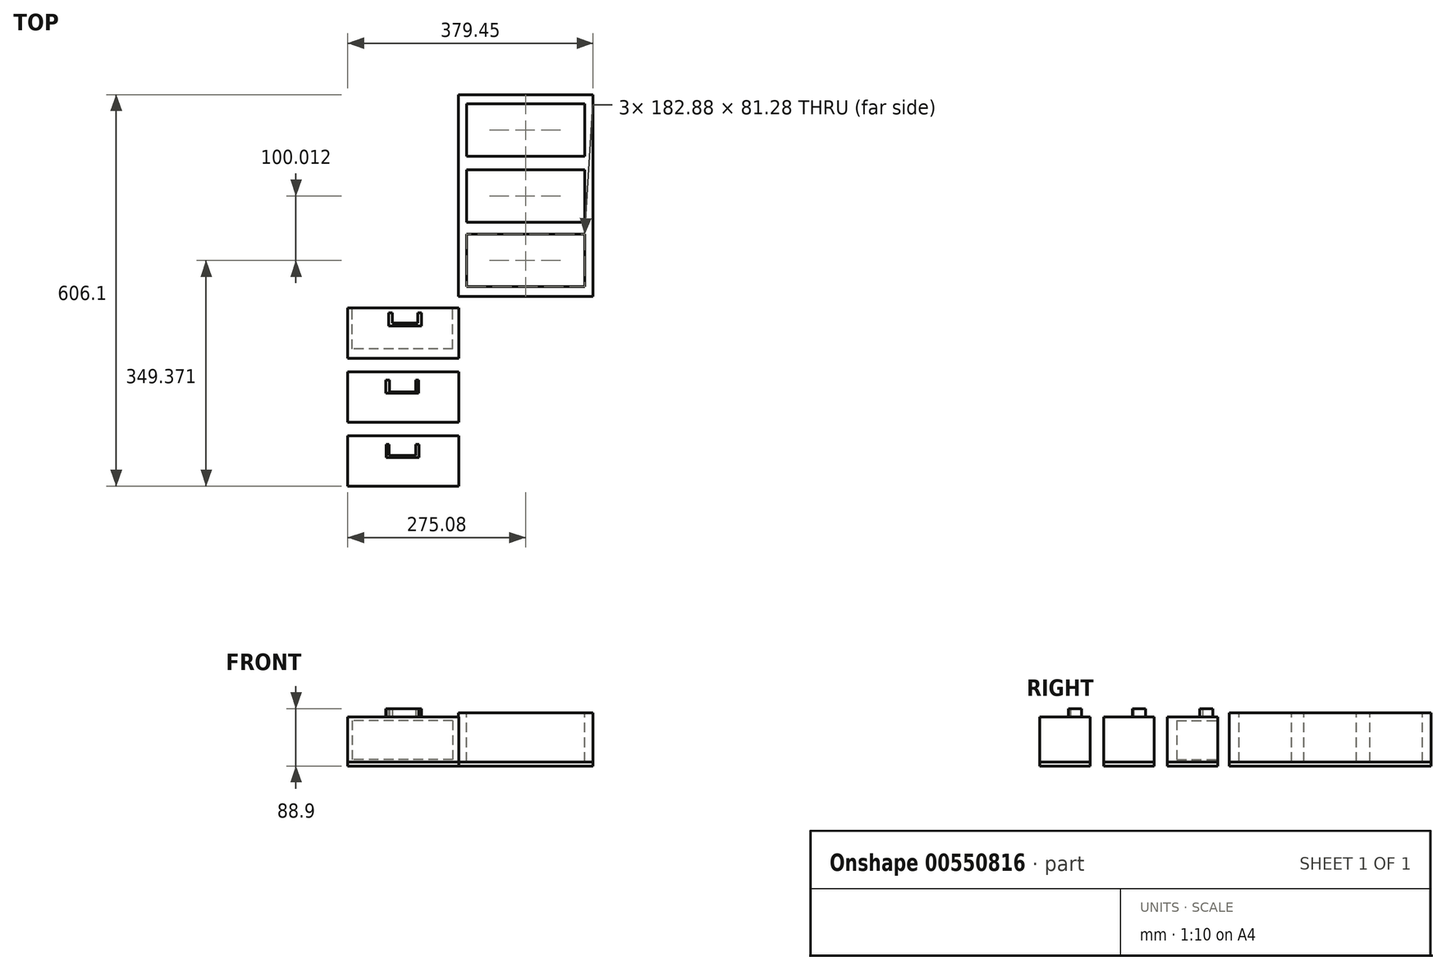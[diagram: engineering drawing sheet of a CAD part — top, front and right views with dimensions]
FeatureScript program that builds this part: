
annotation { "Feature Type Name" : "Feature", "Feature Type Description" : "" }
export const myFeature = defineFeature(function(context is Context, id is Id, definition is map)
    precondition{}
    {
        {
            var Q0;
            Q0=qCreatedBy(makeId("Top.planeOp"),FACE);
            var sketch = newSketch(context, id + "F0", { "sketchPlane" : qUnion([Q0])});
            skPoint(sketch, "E0.middle", {"position": v(0, 0) * mm});
            skLineSegment(sketch, "E1.bottom", {"start": v(208.28, 312.42) * mm, "end": v(0, 312.42) * mm});
            skLineSegment(sketch, "E1.top", {"start": v(208.28, 0) * mm, "end": v(0, 0) * mm});
            skLineSegment(sketch, "E1.left", {"start": v(208.28, 312.42) * mm, "end": v(208.28, 0) * mm});
            skLineSegment(sketch, "E1.right", {"start": v(0, 312.42) * mm, "end": v(0, 0) * mm});
            skLineSegment(sketch, "E2.bottom", {"start": v(12.47, 298.65) * mm, "end": v(195.35, 298.65) * mm});
            skLineSegment(sketch, "E2.top", {"start": v(12.47, 217.37) * mm, "end": v(195.35, 217.37) * mm});
            skLineSegment(sketch, "E2.left", {"start": v(12.47, 298.65) * mm, "end": v(12.47, 217.37) * mm});
            skLineSegment(sketch, "E2.right", {"start": v(195.35, 298.65) * mm, "end": v(195.35, 217.37) * mm});
            skLineSegment(sketch, "E3.bottom", {"start": v(12.47, 196.34) * mm, "end": v(195.35, 196.34) * mm});
            skLineSegment(sketch, "E3.top", {"start": v(12.47, 115.06) * mm, "end": v(195.35, 115.06) * mm});
            skLineSegment(sketch, "E3.left", {"start": v(12.47, 196.34) * mm, "end": v(12.47, 115.06) * mm});
            skLineSegment(sketch, "E3.right", {"start": v(195.35, 196.34) * mm, "end": v(195.35, 115.06) * mm});
            skLineSegment(sketch, "E4.bottom", {"start": v(12.47, 96.33) * mm, "end": v(195.35, 96.33) * mm});
            skLineSegment(sketch, "E4.top", {"start": v(12.47, 15.05) * mm, "end": v(195.35, 15.05) * mm});
            skLineSegment(sketch, "E4.left", {"start": v(12.47, 96.33) * mm, "end": v(12.47, 15.05) * mm});
            skLineSegment(sketch, "E4.right", {"start": v(195.35, 96.33) * mm, "end": v(195.35, 15.05) * mm});
            skSolve(sketch);
        }
        {
            var Q0;
            Q0=makeQuery(id+"F0.imprint","IMPRINT",FACE,{"disambiguationData":[TD([[makeQuery(id+"F0.imprint","IMPRINT",EDGE,{"derivedFrom":sQuery(id+"F0.wireOp",EDGE,"E1.bottom")}),1.0]])]});
            var Q1;
            Q1 = qSketchRegion(id + "F2", true);
            extrude(context, id + "F1", {"entities" : qUnion([Q0, Q1]), "oppositeDirection" : true, "depth" : 76.2 * mm, "offsetDistance" : 25.4 * mm});
        }
        {
            var Q0;
            Q0=makeQuery(id+"F1.opExtrude","CAP_FACE",FACE,{"disambiguationData":[OSD([sQuery(id+"F0.wireOp",EDGE,"E1.bottom"),sQuery(id+"F0.wireOp",EDGE,"E1.top"),sQuery(id+"F0.wireOp",EDGE,"E1.left"),sQuery(id+"F0.wireOp",EDGE,"E1.right")])],"isStart":false});
            var sketch = newSketch(context, id + "F2", { "sketchPlane" : qUnion([Q0])});
            skLineSegment(sketch, "E5.bottom", {"start": v(11.7, 293.68) * mm, "end": v(183.26, 293.68) * mm});
            skLineSegment(sketch, "E5.top", {"start": v(11.7, 215.63) * mm, "end": v(183.26, 215.63) * mm});
            skLineSegment(sketch, "E5.left", {"start": v(11.7, 293.68) * mm, "end": v(11.7, 215.63) * mm});
            skLineSegment(sketch, "E5.right", {"start": v(183.26, 293.68) * mm, "end": v(183.26, 215.63) * mm});
            skLineSegment(sketch, "E6.bottom", {"start": v(11.7, 194.8) * mm, "end": v(183.26, 194.8) * mm});
            skLineSegment(sketch, "E6.top", {"start": v(11.7, 116.74) * mm, "end": v(183.26, 116.74) * mm});
            skLineSegment(sketch, "E6.left", {"start": v(11.7, 194.8) * mm, "end": v(11.7, 116.74) * mm});
            skLineSegment(sketch, "E6.right", {"start": v(183.26, 194.8) * mm, "end": v(183.26, 116.74) * mm});
            skLineSegment(sketch, "E7.bottom", {"start": v(11.7, 95.91) * mm, "end": v(183.26, 95.91) * mm});
            skLineSegment(sketch, "E7.top", {"start": v(11.7, 17.86) * mm, "end": v(183.26, 17.86) * mm});
            skLineSegment(sketch, "E7.left", {"start": v(11.7, 95.91) * mm, "end": v(11.7, 17.86) * mm});
            skLineSegment(sketch, "E7.right", {"start": v(183.26, 95.91) * mm, "end": v(183.26, 17.86) * mm});
            skLineSegment(sketch, "E8.bottom", {"start": v(0, 0) * mm, "end": v(208.28, 0) * mm});
            skLineSegment(sketch, "E8.top", {"start": v(0, -312.42) * mm, "end": v(208.28, -312.42) * mm});
            skLineSegment(sketch, "E8.left", {"start": v(0, 0) * mm, "end": v(0, -312.42) * mm});
            skLineSegment(sketch, "E8.right", {"start": v(208.28, 0) * mm, "end": v(208.28, -312.42) * mm});
            skLineSegment(sketch, "E9.bottom", {"start": v(25.13, 17.86) * mm, "end": v(168.62, 17.86) * mm});
            skSolve(sketch);
        }
        {
            var Q0;
            Q0=makeQuery(id+"F2.imprint","IMPRINT",FACE,{"disambiguationData":[TD([[makeQuery(id+"F2.imprint","IMPRINT",EDGE,{"derivedFrom":sQuery(id+"F2.wireOp",EDGE,"E7.bottom")}),-1.0]])]});
            var Q1;
            Q1=makeQuery(id+"F2.imprint","IMPRINT",FACE,{"disambiguationData":[TD([[makeQuery(id+"F2.imprint","IMPRINT",EDGE,{"derivedFrom":sQuery(id+"F2.wireOp",EDGE,"E6.bottom")}),-1.0]])]});
            var Q2;
            Q2=makeQuery(id+"F2.imprint","IMPRINT",FACE,{"disambiguationData":[TD([[makeQuery(id+"F2.imprint","IMPRINT",EDGE,{"derivedFrom":sQuery(id+"F2.wireOp",EDGE,"E5.bottom")}),-1.0]])]});
            extrude(context, id + "F3", {"entities" : qUnion([Q0, Q1, Q2]), "oppositeDirection" : true, "depth" : 69.85 * mm, "offsetDistance" : 25.4 * mm});
        }
        {
            var Q0;
            Q0 = qSketchRegion(id + "F2", true);
            extrude(context, id + "F4", {"entities" : qUnion([Q0]), "depth" : 6.35 * mm, "offsetDistance" : 25.4 * mm});
        }
        {
            var Q0;
            Q0=makeQuery(id+"F3.opExtrude","CAP_FACE",FACE,{"disambiguationData":[OSD([sQuery(id+"F2.wireOp",EDGE,"E7.bottom"),sQuery(id+"F2.wireOp",EDGE,"E7.top"),sQuery(id+"F2.wireOp",EDGE,"E7.left"),sQuery(id+"F2.wireOp",EDGE,"E7.right")])],"isStart":false});
            var sketch = newSketch(context, id + "F5", { "sketchPlane" : qUnion([Q0])});
            skLineSegment(sketch, "E10.bottom", {"start": v(74.8, -25.28) * mm, "end": v(125.6, -25.28) * mm});
            skLineSegment(sketch, "E10.top", {"start": v(74.8, -45.6) * mm, "end": v(125.6, -45.6) * mm});
            skLineSegment(sketch, "E10.left", {"start": v(74.8, -25.28) * mm, "end": v(74.8, -45.6) * mm});
            skLineSegment(sketch, "E10.right", {"start": v(125.6, -25.28) * mm, "end": v(125.6, -45.6) * mm});
            skLineSegment(sketch, "E11.bottom", {"start": v(80.5, -25.28) * mm, "end": v(119.7, -25.28) * mm});
            skLineSegment(sketch, "E11.top", {"start": v(80.5, -41.56) * mm, "end": v(119.7, -41.56) * mm});
            skLineSegment(sketch, "E11.left", {"start": v(80.5, -25.28) * mm, "end": v(80.5, -41.56) * mm});
            skLineSegment(sketch, "E11.right", {"start": v(119.7, -25.28) * mm, "end": v(119.7, -41.56) * mm});
            skSolve(sketch);
        }
        {
            var Q0;
            Q0=makeQuery(id+"F5.imprint","IMPRINT",FACE,{"disambiguationData":[TD([[makeQuery(id+"F5.imprint","IMPRINT",EDGE,{"derivedFrom":sQuery(id+"F5.wireOp",EDGE,"E10.top")}),1.0]])]});
            extrude(context, id + "F6", {"entities" : qUnion([Q0]), "operationType" : NewBodyOperationType.ADD, "depth" : 12.7 * mm, "offsetDistance" : 25.4 * mm});
        }
        {
            var Q0;
            Q0=makeQuery(id+"F3.opExtrude","CAP_FACE",FACE,{"disambiguationData":[OSD([sQuery(id+"F2.wireOp",EDGE,"E6.bottom"),sQuery(id+"F2.wireOp",EDGE,"E6.top"),sQuery(id+"F2.wireOp",EDGE,"E6.left"),sQuery(id+"F2.wireOp",EDGE,"E6.right")])],"isStart":false});
            var sketch = newSketch(context, id + "F7", { "sketchPlane" : qUnion([Q0])});
            skLineSegment(sketch, "E12.bottom", {"start": v(70.67, -129.82) * mm, "end": v(121.47, -129.82) * mm});
            skLineSegment(sketch, "E12.top", {"start": v(70.67, -150.14) * mm, "end": v(121.47, -150.14) * mm});
            skLineSegment(sketch, "E12.left", {"start": v(70.67, -129.82) * mm, "end": v(70.67, -150.14) * mm});
            skLineSegment(sketch, "E12.right", {"start": v(121.47, -129.82) * mm, "end": v(121.47, -150.14) * mm});
            skLineSegment(sketch, "E13.bottom", {"start": v(75.93, -129.82) * mm, "end": v(116.78, -129.82) * mm});
            skLineSegment(sketch, "E13.top", {"start": v(75.93, -147.93) * mm, "end": v(116.78, -147.93) * mm});
            skLineSegment(sketch, "E13.left", {"start": v(75.93, -129.82) * mm, "end": v(75.93, -147.93) * mm});
            skLineSegment(sketch, "E13.right", {"start": v(116.78, -129.82) * mm, "end": v(116.78, -147.93) * mm});
            skSolve(sketch);
        }
        {
            var Q0;
            Q0=makeQuery(id+"F7.imprint","IMPRINT",FACE,{"disambiguationData":[TD([[makeQuery(id+"F7.imprint","IMPRINT",EDGE,{"derivedFrom":sQuery(id+"F7.wireOp",EDGE,"E12.top")}),1.0]])]});
            extrude(context, id + "F8", {"entities" : qUnion([Q0]), "operationType" : NewBodyOperationType.ADD, "depth" : 12.7 * mm, "offsetDistance" : 25.4 * mm});
        }
        {
            var Q0;
            Q0=makeQuery(id+"F3.opExtrude","CAP_FACE",FACE,{"disambiguationData":[OSD([sQuery(id+"F2.wireOp",EDGE,"E5.bottom"),sQuery(id+"F2.wireOp",EDGE,"E5.top"),sQuery(id+"F2.wireOp",EDGE,"E5.left"),sQuery(id+"F2.wireOp",EDGE,"E5.right")])],"isStart":false});
            var sketch = newSketch(context, id + "F9", { "sketchPlane" : qUnion([Q0])});
            skLineSegment(sketch, "E14.bottom", {"start": v(70.8, -229.1) * mm, "end": v(121.6, -229.1) * mm});
            skLineSegment(sketch, "E14.top", {"start": v(70.8, -249.43) * mm, "end": v(121.6, -249.43) * mm});
            skLineSegment(sketch, "E14.left", {"start": v(70.8, -229.1) * mm, "end": v(70.8, -249.43) * mm});
            skLineSegment(sketch, "E14.right", {"start": v(121.6, -229.1) * mm, "end": v(121.6, -249.43) * mm});
            skLineSegment(sketch, "E15.bottom", {"start": v(75.68, -229.1) * mm, "end": v(116.79, -229.1) * mm});
            skLineSegment(sketch, "E15.top", {"start": v(75.68, -246.1) * mm, "end": v(116.79, -246.1) * mm});
            skLineSegment(sketch, "E15.left", {"start": v(75.68, -229.1) * mm, "end": v(75.68, -246.1) * mm});
            skLineSegment(sketch, "E15.right", {"start": v(116.79, -229.1) * mm, "end": v(116.79, -246.1) * mm});
            skSolve(sketch);
        }
        {
            var Q0;
            Q0=makeQuery(id+"F9.imprint","IMPRINT",FACE,{"disambiguationData":[TD([[makeQuery(id+"F9.imprint","IMPRINT",EDGE,{"derivedFrom":sQuery(id+"F9.wireOp",EDGE,"E14.top")}),1.0]])]});
            extrude(context, id + "F10", {"entities" : qUnion([Q0]), "operationType" : NewBodyOperationType.ADD, "depth" : 12.7 * mm, "offsetDistance" : 25.4 * mm});
        }
        {
            var Q0;
            Q0=makeQuery(id+"F1.opExtrude","SWEPT_BODY",BODY,{"disambiguationData":[OSD([sQuery(id+"F0.wireOp",EDGE,"E1.bottom"),sQuery(id+"F0.wireOp",EDGE,"E1.top"),sQuery(id+"F0.wireOp",EDGE,"E1.left"),sQuery(id+"F0.wireOp",EDGE,"E1.right"),sQuery(id+"F0.wireOp",EDGE,"E2.bottom"),sQuery(id+"F0.wireOp",EDGE,"E2.top"),sQuery(id+"F0.wireOp",EDGE,"E2.left"),sQuery(id+"F0.wireOp",EDGE,"E2.right"),sQuery(id+"F0.wireOp",EDGE,"E3.bottom"),sQuery(id+"F0.wireOp",EDGE,"E3.top"),sQuery(id+"F0.wireOp",EDGE,"E3.left"),sQuery(id+"F0.wireOp",EDGE,"E3.right"),sQuery(id+"F0.wireOp",EDGE,"E4.bottom"),sQuery(id+"F0.wireOp",EDGE,"E4.top"),sQuery(id+"F0.wireOp",EDGE,"E4.left"),sQuery(id+"F0.wireOp",EDGE,"E4.right")])]});
            var Q1;
            Q1=makeQuery(id+"F4.opExtrude","SWEPT_BODY",BODY,{"disambiguationData":[OSD([sQuery(id+"F2.wireOp",EDGE,"E8.bottom"),sQuery(id+"F2.wireOp",EDGE,"E8.top"),sQuery(id+"F2.wireOp",EDGE,"E8.left"),sQuery(id+"F2.wireOp",EDGE,"E8.right")])]});
            var Q2;
            Q2=sQuery(id+"F0.wireOp",VERTEX,"E4.left.end");
            var Q3;
            Q3=sQuery(id+"F0.wireOp",VERTEX,"E4.right.end");
            transform(context, id + "F11", {"entities" : qUnion([Q0, Q1]), "transformType" : TransformType.TRANSLATION_ENTITY, "oppositeDirectionEntity" : false, "transformLine" : qUnion([Q2, Q3]), "makeCopy" : false});
        }
        {
            var Q0;
            Q0=makeQuery(id+"F3.opExtrude","SWEPT_FACE",FACE,{"disambiguationData":[OSD([sQuery(id+"F2.wireOp",EDGE,"E7.top"),sQuery(id+"F2.wireOp",EDGE,"E9.bottom")])]});
            var sketch = newSketch(context, id + "F12", { "sketchPlane" : qUnion([Q0])});
            skLineSegment(sketch, "E16.bottom", {"start": v(-174.23, -11.93) * mm, "end": v(-18.07, -11.93) * mm});
            skLineSegment(sketch, "E16.top", {"start": v(-174.23, -72.63) * mm, "end": v(-18.07, -72.63) * mm});
            skLineSegment(sketch, "E16.left", {"start": v(-174.23, -11.93) * mm, "end": v(-174.23, -72.63) * mm});
            skLineSegment(sketch, "E16.right", {"start": v(-18.07, -11.93) * mm, "end": v(-18.07, -72.63) * mm});
            skSolve(sketch);
        }
        {
            var Q0;
            Q0=makeQuery(id+"F12.imprint","IMPRINT",FACE,{"disambiguationData":[TD([[makeQuery(id+"F12.imprint","IMPRINT",EDGE,{"derivedFrom":sQuery(id+"F12.wireOp",EDGE,"E16.bottom")}),-1.0]])]});
            extrude(context, id + "F13", {"entities" : qUnion([Q0]), "operationType" : NewBodyOperationType.REMOVE, "oppositeDirection" : true, "depth" : 63.5 * mm, "offsetDistance" : 25.4 * mm});
        }
    });
